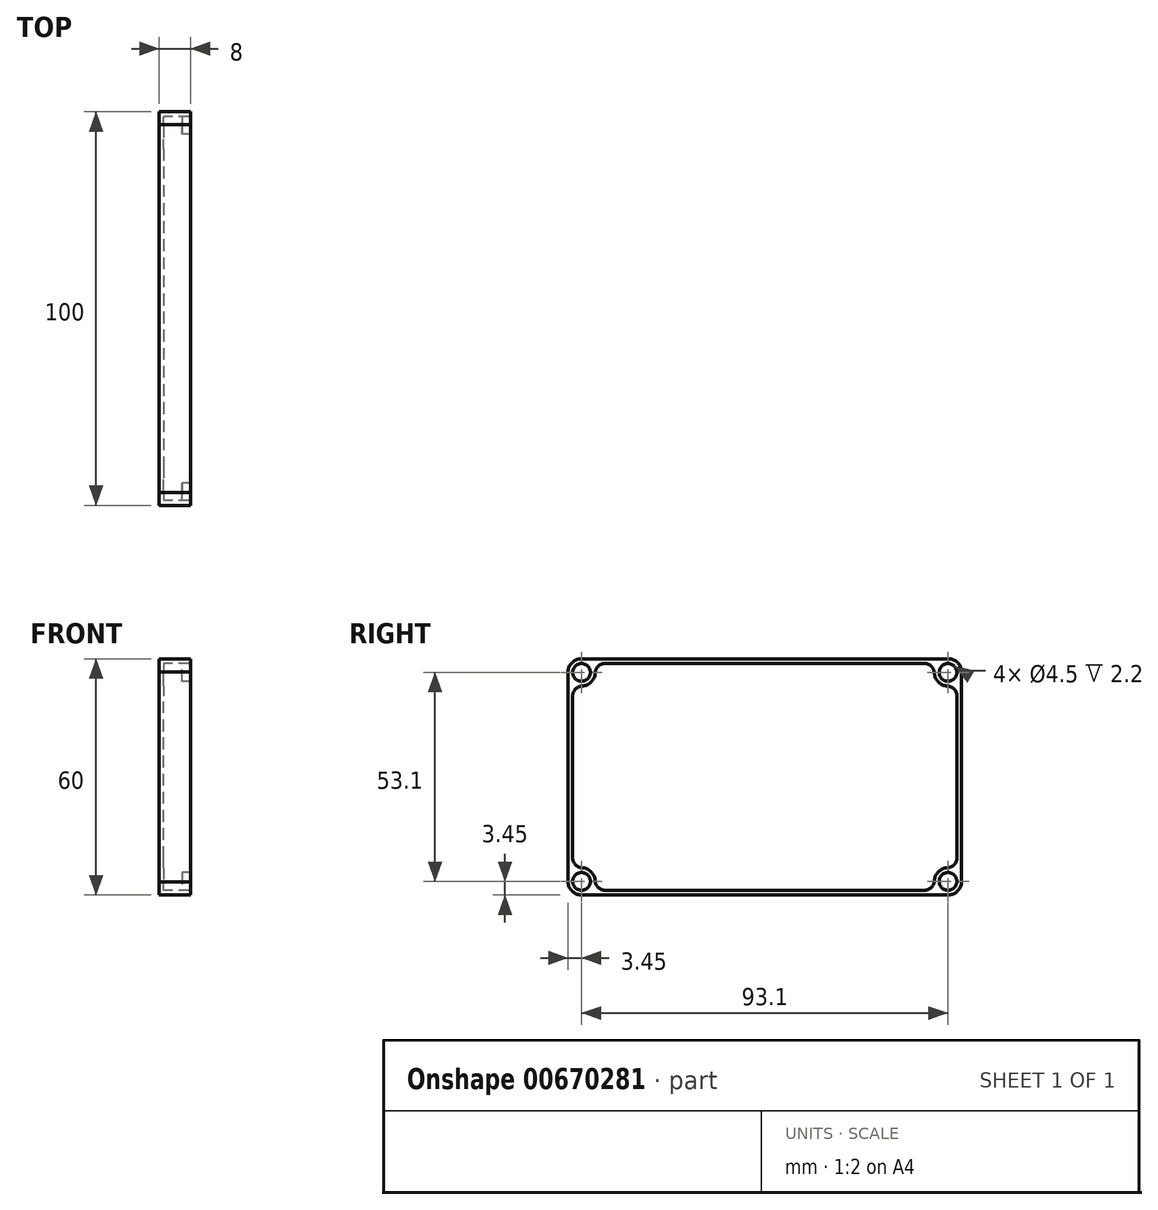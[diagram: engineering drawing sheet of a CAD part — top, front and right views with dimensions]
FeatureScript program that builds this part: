
annotation { "Feature Type Name" : "Feature", "Feature Type Description" : "" }
export const myFeature = defineFeature(function(context is Context, id is Id, definition is map)
    precondition{}
    {
        {
            var Q0;
            Q0=qCreatedBy(makeId("Right.planeOp"),FACE);
            var sketch = newSketch(context, id + "F0", { "sketchPlane" : qUnion([Q0])});
            skLineSegment(sketch, "E0.bottom", {"start": v(0, 0) * mm, "end": v(-50, 0) * mm});
            skLineSegment(sketch, "E0.top", {"start": v(0, 30) * mm, "end": v(-46.7, 30) * mm});
            skLineSegment(sketch, "E0.left", {"start": v(0, 0) * mm, "end": v(0, 30) * mm});
            skLineSegment(sketch, "E0.right", {"start": v(-50, 0) * mm, "end": v(-50, 26.7) * mm});
            skCircle(sketch, "E1", {"center": v(-46.55, 26.55) * mm, "radius": 2.25 * mm});
            skArc(sketch, "E2", {"start": v(-46.4, 23.1) * mm, "mid": v(-44.1, 24.1) * mm, "end": v(-43.1, 26.4) * mm});
            skLineSegment(sketch, "E3", {"start": v(0, 28.8) * mm, "end": v(-40.6, 28.8) * mm});
            skLineSegment(sketch, "E4", {"start": v(-48.8, 0) * mm, "end": v(-48.8, 20.6) * mm});
            skArc(sketch, "E5.trimOffspring", {"start": v(-46.4, 30) * mm, "mid": v(-49, 29) * mm, "end": v(-50, 26.4) * mm});
            skPoint(sketch, "E6.visualSharp", {"position": v(-43.93, 28.8) * mm});
            skArc(sketch, "E6.filletArc", {"start": v(-40.6, 28.8) * mm, "mid": v(-42.33, 28.1) * mm, "end": v(-43.1, 26.4) * mm});
            skPoint(sketch, "E7.visualSharp", {"position": v(-48.8, 23.93) * mm});
            skArc(sketch, "E7.filletArc", {"start": v(-46.4, 23.1) * mm, "mid": v(-48.1, 22.33) * mm, "end": v(-48.8, 20.6) * mm});
            skSolve(sketch);
        }
        {
            var Q0;
            Q0=makeQuery(id+"F0.imprint","IMPRINT",FACE,{"disambiguationData":[TD([[makeQuery(id+"F0.imprint","IMPRINT",EDGE,{"derivedFrom":sQuery(id+"F0.wireOp",EDGE,"E1")}),-1.0]])]});
            extrude(context, id + "F1", {"entities" : qUnion([Q0]), "depth" : 8 * mm, "offsetDistance" : 25 * mm});
        }
        {
            var Q0;
            Q0=makeQuery(id+"F0.imprint","IMPRINT",FACE,{"disambiguationData":[TD([[makeQuery(id+"F0.imprint","IMPRINT",EDGE,{"derivedFrom":sQuery(id+"F0.wireOp",EDGE,"E2")}),-1.0]])]});
            extrude(context, id + "F2", {"entities" : qUnion([Q0]), "operationType" : NewBodyOperationType.ADD, "depth" : 1.2 * mm, "offsetDistance" : 25 * mm});
        }
        {
            var Q0;
            Q0=makeQuery(id+"F0.imprint","IMPRINT",FACE,{"disambiguationData":[TD([[makeQuery(id+"F0.imprint","IMPRINT",EDGE,{"derivedFrom":sQuery(id+"F0.wireOp",EDGE,"E1")}),1.0]])]});
            extrude(context, id + "F3", {"entities" : qUnion([Q0]), "operationType" : NewBodyOperationType.ADD, "depth" : 5.8 * mm, "offsetDistance" : 25 * mm});
        }
        {
            var Q0;
            Q0=makeQuery(id+"F1.opExtrude","SWEPT_BODY",BODY,{"disambiguationData":[OSD([sQuery(id+"F0.wireOp",EDGE,"E0.bottom"),sQuery(id+"F0.wireOp",EDGE,"E0.top"),sQuery(id+"F0.wireOp",EDGE,"E0.left"),sQuery(id+"F0.wireOp",EDGE,"E0.right"),sQuery(id+"F0.wireOp",EDGE,"E1"),sQuery(id+"F0.wireOp",EDGE,"E2"),sQuery(id+"F0.wireOp",EDGE,"E3"),sQuery(id+"F0.wireOp",EDGE,"E4"),sQuery(id+"F0.wireOp",EDGE,"E5.trimOffspring"),sQuery(id+"F0.wireOp",EDGE,"E6.filletArc"),sQuery(id+"F0.wireOp",EDGE,"E7.filletArc")])]});
            var Q1;
            Q1=qCreatedBy(makeId("Front.planeOp"),FACE);
            mirror(context, id + "F4", {"operationType" : NewBodyOperationType.ADD, "entities" : qUnion([Q0]), "mirrorPlane" : qUnion([Q1])});
        }
        {
            var Q0;
            Q0=makeQuery(id+"F1.opExtrude","SWEPT_BODY",BODY,{"disambiguationData":[OSD([sQuery(id+"F0.wireOp",EDGE,"E0.bottom"),sQuery(id+"F0.wireOp",EDGE,"E0.top"),sQuery(id+"F0.wireOp",EDGE,"E0.left"),sQuery(id+"F0.wireOp",EDGE,"E0.right"),sQuery(id+"F0.wireOp",EDGE,"E1"),sQuery(id+"F0.wireOp",EDGE,"E2"),sQuery(id+"F0.wireOp",EDGE,"E3"),sQuery(id+"F0.wireOp",EDGE,"E4"),sQuery(id+"F0.wireOp",EDGE,"E5.trimOffspring"),sQuery(id+"F0.wireOp",EDGE,"E6.filletArc"),sQuery(id+"F0.wireOp",EDGE,"E7.filletArc")])]});
            var Q1;
            Q1=qCreatedBy(makeId("Top.planeOp"),FACE);
            mirror(context, id + "F5", {"operationType" : NewBodyOperationType.ADD, "entities" : qUnion([Q0]), "mirrorPlane" : qUnion([Q1])});
        }
    });
